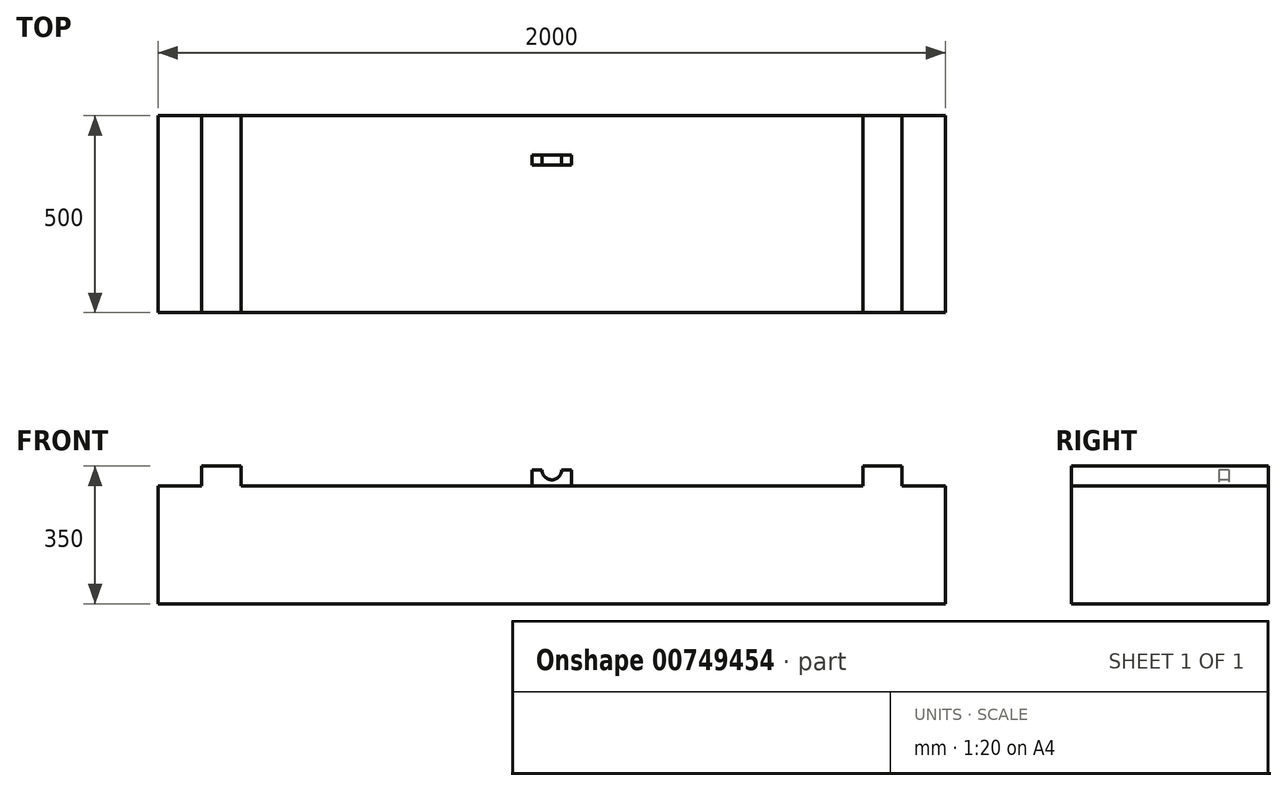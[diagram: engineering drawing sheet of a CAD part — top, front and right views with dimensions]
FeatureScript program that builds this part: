
annotation { "Feature Type Name" : "Feature", "Feature Type Description" : "" }
export const myFeature = defineFeature(function(context is Context, id is Id, definition is map)
    precondition{}
    {
        {
            var Q0;
            Q0=qCreatedBy(makeId("Front.planeOp"),FACE);
            var sketch = newSketch(context, id + "F0", { "sketchPlane" : qUnion([Q0])});
            skLineSegment(sketch, "E0.bottom", {"start": v(-1000, 0) * mm, "end": v(1000, 0) * mm});
            skLineSegment(sketch, "E0.top", {"start": v(-1000, -300) * mm, "end": v(1000, -300) * mm});
            skLineSegment(sketch, "E0.left", {"start": v(-1000, 0) * mm, "end": v(-1000, -300) * mm});
            skLineSegment(sketch, "E0.right", {"start": v(1000, 0) * mm, "end": v(1000, -300) * mm});
            skSolve(sketch);
        }
        {
            var Q0;
            Q0 = qSketchRegion(id + "F0", true);
            extrude(context, id + "F1", {"entities" : qUnion([Q0]), "depth" : 500 * mm, "offsetDistance" : 25 * mm, "symmetric" : true});
        }
        {
            var Q0;
            Q0=makeQuery(id+"F1.opExtrude","SWEPT_FACE",FACE,{"disambiguationData":[OSD([sQuery(id+"F0.wireOp",EDGE,"E0.bottom")])]});
            var sketch = newSketch(context, id + "F2", { "sketchPlane" : qUnion([Q0])});
            skLineSegment(sketch, "E1.bottom", {"start": v(790, 250) * mm, "end": v(890, 250) * mm});
            skLineSegment(sketch, "E1.top", {"start": v(790, -250) * mm, "end": v(890, -250) * mm});
            skLineSegment(sketch, "E1.left", {"start": v(790, 250) * mm, "end": v(790, -250) * mm});
            skLineSegment(sketch, "E1.right", {"start": v(890, 250) * mm, "end": v(890, -250) * mm});
            skLineSegment(sketch, "E2.MirrorCS", {"start": v(-790, 250) * mm, "end": v(-790, -250) * mm});
            skLineSegment(sketch, "E3.MirrorCS", {"start": v(-890, 250) * mm, "end": v(-890, -250) * mm});
            skLineSegment(sketch, "E4.MirrorCS", {"start": v(-790, -250) * mm, "end": v(-890, -250) * mm});
            skLineSegment(sketch, "E5.MirrorCS", {"start": v(-790, 250) * mm, "end": v(-890, 250) * mm});
            skSolve(sketch);
        }
        {
            var Q0;
            Q0=makeQuery(id+"F2.imprint","IMPRINT",FACE,{"disambiguationData":[TD([[makeQuery(id+"F2.imprint","IMPRINT",EDGE,{"derivedFrom":sQuery(id+"F2.wireOp",EDGE,"E1.bottom")}),-1.0]])]});
            var Q1;
            Q1=makeQuery(id+"F2.imprint","IMPRINT",FACE,{"disambiguationData":[TD([[makeQuery(id+"F2.imprint","IMPRINT",EDGE,{"derivedFrom":sQuery(id+"F2.wireOp",EDGE,"E2.MirrorCS")}),-1.0]])]});
            extrude(context, id + "F3", {"entities" : qUnion([Q0, Q1]), "operationType" : NewBodyOperationType.ADD, "depth" : 50 * mm, "offsetDistance" : 25 * mm});
        }
        {
            var Q0;
            Q0=makeQuery(id+"F3.boolean.opBoolean","MERGE",FACE,{"derivedFrom":[makeQuery(id+"F1.opExtrude","CAP_FACE",FACE,{"disambiguationData":[OSD([sQuery(id+"F0.wireOp",EDGE,"E0.bottom"),sQuery(id+"F0.wireOp",EDGE,"E0.top"),sQuery(id+"F0.wireOp",EDGE,"E0.left"),sQuery(id+"F0.wireOp",EDGE,"E0.right")])],"isStart":false}),makeQuery(id+"F3.opExtrude","SWEPT_FACE",FACE,{"disambiguationData":[OSD([sQuery(id+"F2.wireOp",EDGE,"E1.top")])]})]});
            var sketch = newSketch(context, id + "F4", { "sketchPlane" : qUnion([Q0])});
            skArc(sketch, "E6", {"start": v(-25, 40) * mm, "mid": v(0, 15) * mm, "end": v(25, 40) * mm});
            skLineSegment(sketch, "E7.bottom", {"start": v(-50, 40) * mm, "end": v(-25, 40) * mm});
            skLineSegment(sketch, "E7.top", {"start": v(-50, 0) * mm, "end": v(50, 0) * mm});
            skLineSegment(sketch, "E7.left", {"start": v(-50, 40) * mm, "end": v(-50, 0) * mm});
            skLineSegment(sketch, "E7.right", {"start": v(50, 40) * mm, "end": v(50, 0) * mm});
            skLineSegment(sketch, "E8.trimOffspring", {"start": v(25, 40) * mm, "end": v(50, 40) * mm});
            skSolve(sketch);
        }
        {
            var Q0;
            Q0=makeQuery(id+"F4.imprint","IMPRINT",FACE,{"disambiguationData":[TD([[makeQuery(id+"F4.imprint","IMPRINT",EDGE,{"derivedFrom":sQuery(id+"F4.wireOp",EDGE,"E6")}),-1.0]])]});
            extrude(context, id + "F5", {"entities" : qUnion([Q0]), "operationType" : NewBodyOperationType.ADD, "oppositeDirection" : true, "depth" : 400 * mm, "offsetDistance" : 25 * mm, "hasSecondDirection" : true, "secondDirectionOppositeDirection" : false, "secondDirectionDepth" : -375 * mm});
        }
    });
